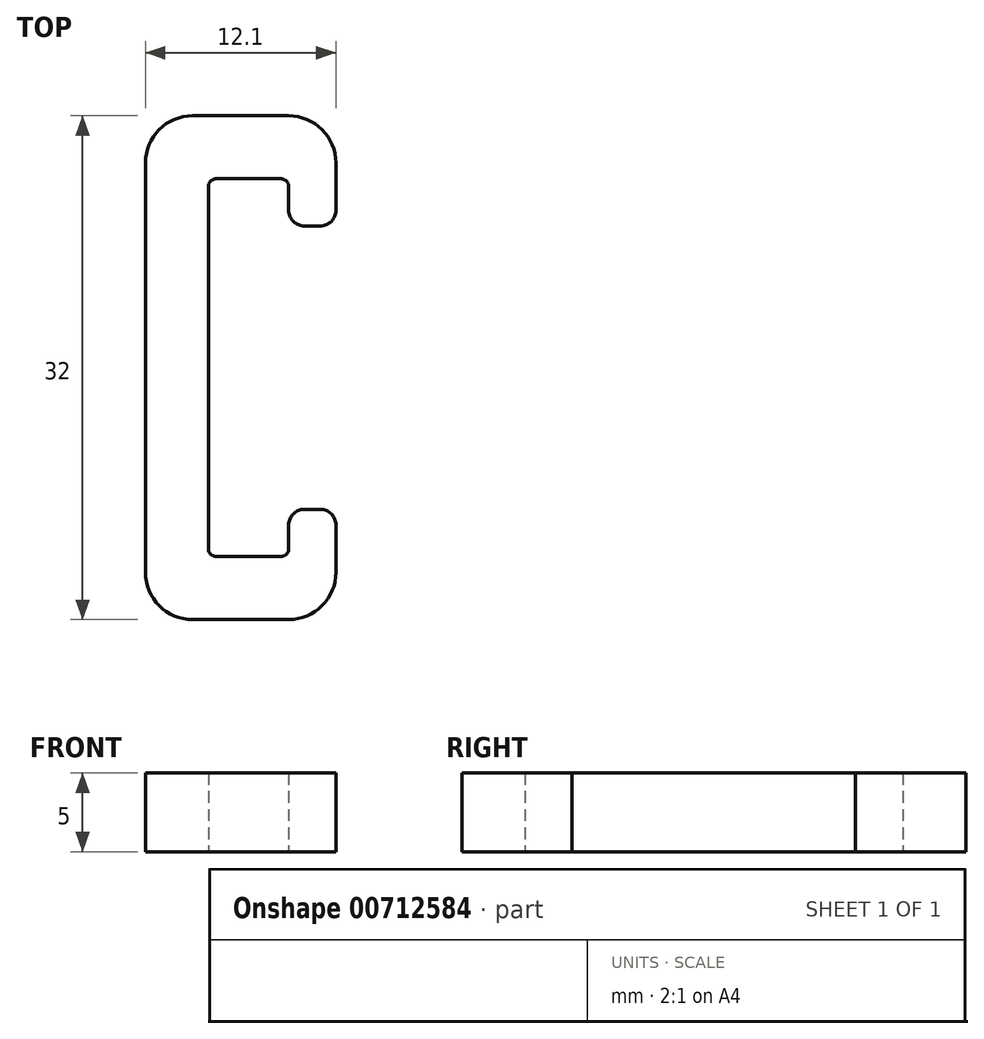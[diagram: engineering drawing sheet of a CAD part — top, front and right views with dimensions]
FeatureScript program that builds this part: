
annotation { "Feature Type Name" : "Feature", "Feature Type Description" : "" }
export const myFeature = defineFeature(function(context is Context, id is Id, definition is map)
    precondition{}
    {
        {
            var Q0;
            Q0=qCreatedBy(makeId("Top.planeOp"),FACE);
            var sketch = newSketch(context, id + "F0", { "sketchPlane" : qUnion([Q0])});
            skLineSegment(sketch, "E0", {"start": v(0, 0) * mm, "end": v(0, 24) * mm});
            skLineSegment(sketch, "E1", {"start": v(0, 24) * mm, "end": v(5.1, 24) * mm});
            skLineSegment(sketch, "E2", {"start": v(5.1, 24) * mm, "end": v(5.1, 21) * mm});
            skLineSegment(sketch, "E3", {"start": v(5.1, 21) * mm, "end": v(8.1, 21) * mm});
            skLineSegment(sketch, "E4", {"start": v(8.1, 21) * mm, "end": v(8.1, 28) * mm});
            skLineSegment(sketch, "E5", {"start": v(8.1, 28) * mm, "end": v(-4, 28) * mm});
            skLineSegment(sketch, "E6", {"start": v(-4, 28) * mm, "end": v(-4, -4) * mm});
            skLineSegment(sketch, "E7", {"start": v(-4, -4) * mm, "end": v(8.1, -4) * mm});
            skLineSegment(sketch, "E8", {"start": v(8.1, -4) * mm, "end": v(8.1, 3) * mm});
            skLineSegment(sketch, "E9", {"start": v(8.1, 3) * mm, "end": v(5.1, 3) * mm});
            skLineSegment(sketch, "E10", {"start": v(5.1, 3) * mm, "end": v(5.1, 0) * mm});
            skLineSegment(sketch, "E11", {"start": v(5.1, 0) * mm, "end": v(0, 0) * mm});
            skSolve(sketch);
        }
        {
            var Q0;
            Q0=makeQuery(id+"F0.imprint","IMPRINT",FACE,{"disambiguationData":[TD([[makeQuery(id+"F0.imprint","IMPRINT",EDGE,{"derivedFrom":sQuery(id+"F0.wireOp",EDGE,"E0")}),1.0]])]});
            extrude(context, id + "F1", {"entities" : qUnion([Q0]), "depth" : 5 * mm, "offsetDistance" : 25 * mm});
        }
        {
            var Q0;
            Q0=makeQuery(id+"F1.opExtrude","SWEPT_EDGE",EDGE,{"disambiguationData":[OSD([sQuery(id+"F0.wireOp",EDGE,"E5"),sQuery(id+"F0.wireOp",EDGE,"E6")])]});
            var Q1;
            Q1=makeQuery(id+"F1.opExtrude","SWEPT_EDGE",EDGE,{"disambiguationData":[OSD([sQuery(id+"F0.wireOp",EDGE,"E6"),sQuery(id+"F0.wireOp",EDGE,"E7")])]});
            var Q2;
            Q2=makeQuery(id+"F1.opExtrude","SWEPT_EDGE",EDGE,{"disambiguationData":[OSD([sQuery(id+"F0.wireOp",EDGE,"E7"),sQuery(id+"F0.wireOp",EDGE,"E8")])]});
            var Q3;
            Q3=makeQuery(id+"F1.opExtrude","SWEPT_EDGE",EDGE,{"disambiguationData":[OSD([sQuery(id+"F0.wireOp",EDGE,"E4"),sQuery(id+"F0.wireOp",EDGE,"E5")])]});
            fillet(context, id + "F2", {"entities" : qUnion([Q0, Q1, Q2, Q3]), "radius" : 3 * mm, "tangentPropagation" : true, "allowEdgeOverflow" : false});
        }
        {
            var Q0;
            Q0=makeQuery(id+"F1.opExtrude","SWEPT_EDGE",EDGE,{"disambiguationData":[OSD([sQuery(id+"F0.wireOp",EDGE,"E0"),sQuery(id+"F0.wireOp",EDGE,"E1")])]});
            var Q1;
            Q1=makeQuery(id+"F1.opExtrude","SWEPT_EDGE",EDGE,{"disambiguationData":[OSD([sQuery(id+"F0.wireOp",EDGE,"E1"),sQuery(id+"F0.wireOp",EDGE,"E2")])]});
            var Q2;
            Q2=makeQuery(id+"F1.opExtrude","SWEPT_EDGE",EDGE,{"disambiguationData":[OSD([sQuery(id+"F0.wireOp",EDGE,"E0"),sQuery(id+"F0.wireOp",EDGE,"E11")])]});
            var Q3;
            Q3=makeQuery(id+"F1.opExtrude","SWEPT_EDGE",EDGE,{"disambiguationData":[OSD([sQuery(id+"F0.wireOp",EDGE,"E10"),sQuery(id+"F0.wireOp",EDGE,"E11")])]});
            fillet(context, id + "F3", {"entities" : qUnion([Q0, Q1, Q2, Q3]), "radius" : 0.5 * mm, "tangentPropagation" : true, "allowEdgeOverflow" : false});
        }
        {
            var Q0;
            Q0=makeQuery(id+"F1.opExtrude","SWEPT_EDGE",EDGE,{"disambiguationData":[OSD([sQuery(id+"F0.wireOp",EDGE,"E2"),sQuery(id+"F0.wireOp",EDGE,"E3")])]});
            var Q1;
            Q1=makeQuery(id+"F1.opExtrude","SWEPT_EDGE",EDGE,{"disambiguationData":[OSD([sQuery(id+"F0.wireOp",EDGE,"E9"),sQuery(id+"F0.wireOp",EDGE,"E10")])]});
            var Q2;
            Q2=makeQuery(id+"F1.opExtrude","SWEPT_EDGE",EDGE,{"disambiguationData":[OSD([sQuery(id+"F0.wireOp",EDGE,"E3"),sQuery(id+"F0.wireOp",EDGE,"E4")])]});
            var Q3;
            Q3=makeQuery(id+"F1.opExtrude","SWEPT_EDGE",EDGE,{"disambiguationData":[OSD([sQuery(id+"F0.wireOp",EDGE,"E8"),sQuery(id+"F0.wireOp",EDGE,"E9")])]});
            fillet(context, id + "F4", {"entities" : qUnion([Q0, Q1, Q2, Q3]), "radius" : 1 * mm, "tangentPropagation" : true, "allowEdgeOverflow" : false});
        }
    });
